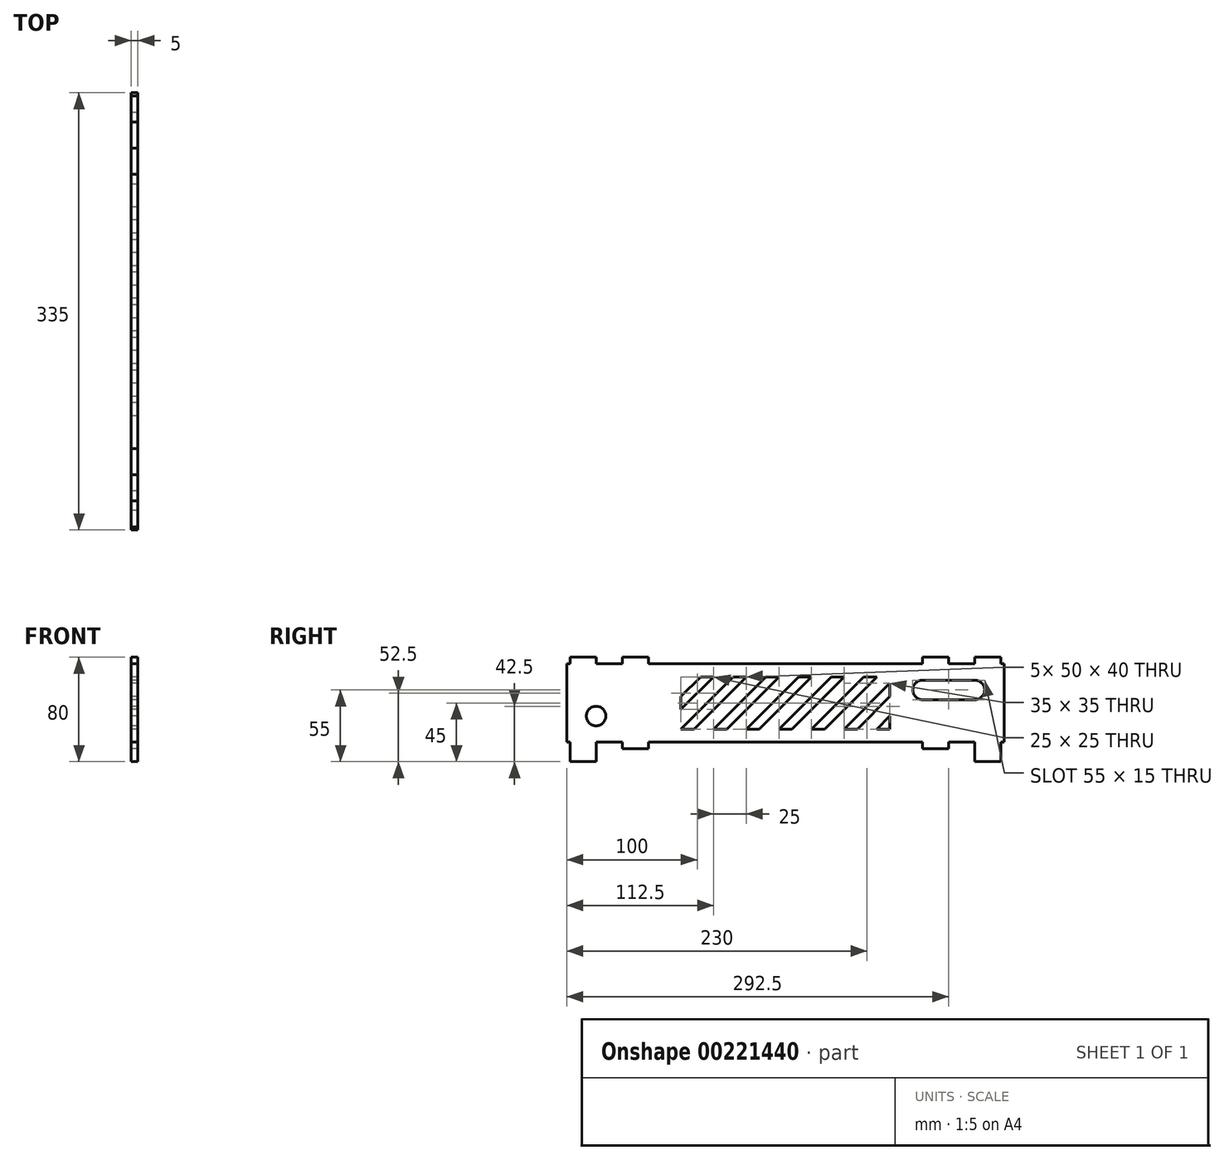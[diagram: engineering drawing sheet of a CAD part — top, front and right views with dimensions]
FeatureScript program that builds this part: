
annotation { "Feature Type Name" : "Feature", "Feature Type Description" : "" }
export const myFeature = defineFeature(function(context is Context, id is Id, definition is map)
    precondition{}
    {
        {
            assignVariable(context, id + "F0", {"name" : "thickness", "anyValue" : 5 * mm});
        }
        {
            var Q0;
            Q0=qCreatedBy(makeId("Right.planeOp"),FACE);
            var sketch = newSketch(context, id + "F1", { "sketchPlane" : qUnion([Q0])});
            skLineSegment(sketch, "E0.bottom", {"start": v(0, 0) * mm, "end": v(335, 0) * mm});
            skLineSegment(sketch, "E0.top", {"start": v(0, 60) * mm, "end": v(335, 60) * mm});
            skLineSegment(sketch, "E0.left", {"start": v(0, 0) * mm, "end": v(0, 60) * mm});
            skLineSegment(sketch, "E0.right", {"start": v(335, 0) * mm, "end": v(335, 60) * mm});
            skLineSegment(sketch, "E1", {"start": v(332.5, 0) * mm, "end": v(332.5, -15) * mm});
            skLineSegment(sketch, "E2", {"start": v(332.5, -15) * mm, "end": v(312.5, -15) * mm});
            skLineSegment(sketch, "E3", {"start": v(312.5, -15) * mm, "end": v(312.5, 0) * mm});
            skLineSegment(sketch, "E4", {"start": v(292.5, 0) * mm, "end": v(292.5, -5) * mm});
            skLineSegment(sketch, "E5", {"start": v(292.5, -5) * mm, "end": v(272.5, -5) * mm});
            skLineSegment(sketch, "E6", {"start": v(272.5, -5) * mm, "end": v(272.5, 0) * mm});
            skLineSegment(sketch, "E7", {"start": v(167.5, 60) * mm, "end": v(167.5, 0) * mm, "construction": true});
            skLineSegment(sketch, "E8", {"start": v(0, 30) * mm, "end": v(335, 30) * mm, "construction": true});
            skLineSegment(sketch, "E9.MirrorCS", {"start": v(62.5, -5) * mm, "end": v(62.5, 0) * mm});
            skLineSegment(sketch, "E10.MirrorCS", {"start": v(42.5, 0) * mm, "end": v(42.5, -5) * mm});
            skLineSegment(sketch, "E11.MirrorCS", {"start": v(42.5, -5) * mm, "end": v(62.5, -5) * mm});
            skLineSegment(sketch, "E12.MirrorCS", {"start": v(2.5, 0) * mm, "end": v(2.5, -15) * mm});
            skLineSegment(sketch, "E13.MirrorCS", {"start": v(2.5, -15) * mm, "end": v(22.5, -15) * mm});
            skLineSegment(sketch, "E14.MirrorCS", {"start": v(22.5, -15) * mm, "end": v(22.5, 0) * mm});
            skLineSegment(sketch, "E15.MirrorCS", {"start": v(62.5, 65) * mm, "end": v(62.5, 60) * mm});
            skLineSegment(sketch, "E16.MirrorCS", {"start": v(42.5, 60) * mm, "end": v(42.5, 65) * mm});
            skLineSegment(sketch, "E17.MirrorCS", {"start": v(42.5, 65) * mm, "end": v(62.5, 65) * mm});
            skLineSegment(sketch, "E18.MirrorCS", {"start": v(272.5, 65) * mm, "end": v(272.5, 60) * mm});
            skLineSegment(sketch, "E19.MirrorCS", {"start": v(292.5, 60) * mm, "end": v(292.5, 65) * mm});
            skLineSegment(sketch, "E20.MirrorCS", {"start": v(292.5, 65) * mm, "end": v(272.5, 65) * mm});
            skLineSegment(sketch, "E21", {"start": v(2.5, 60) * mm, "end": v(2.5, 65) * mm});
            skLineSegment(sketch, "E22", {"start": v(2.5, 65) * mm, "end": v(22.5, 65) * mm});
            skLineSegment(sketch, "E23", {"start": v(22.5, 65) * mm, "end": v(22.5, 60) * mm});
            skLineSegment(sketch, "E24.MirrorCS", {"start": v(332.5, 65) * mm, "end": v(312.5, 65) * mm});
            skLineSegment(sketch, "E25.MirrorCS", {"start": v(312.5, 65) * mm, "end": v(312.5, 60) * mm});
            skLineSegment(sketch, "E26.MirrorCS", {"start": v(332.5, 60) * mm, "end": v(332.5, 65) * mm});
            skLineSegment(sketch, "E27", {"start": v(272.5, 40) * mm, "end": v(312.5, 40) * mm, "construction": true});
            skArc(sketch, "E28.0.startCap", {"start": v(272.5, 32.5) * mm, "mid": v(265, 40) * mm, "end": v(272.5, 47.5) * mm});
            skArc(sketch, "E28.0.endCap", {"start": v(312.5, 47.5) * mm, "mid": v(320, 40) * mm, "end": v(312.5, 32.5) * mm});
            skLineSegment(sketch, "E28.0.left", {"start": v(272.5, 47.5) * mm, "end": v(312.5, 47.5) * mm});
            skLineSegment(sketch, "E28.0.right", {"start": v(272.5, 32.5) * mm, "end": v(312.5, 32.5) * mm});
            skCircle(sketch, "E29", {"center": v(22.5, 20) * mm, "radius": 7.5 * mm});
            skLineSegment(sketch, "E30.bottom", {"start": v(87.5, 50) * mm, "end": v(247.5, 50) * mm, "construction": true});
            skLineSegment(sketch, "E30.top", {"start": v(87.5, 10) * mm, "end": v(247.5, 10) * mm, "construction": true});
            skLineSegment(sketch, "E30.left", {"start": v(87.5, 50) * mm, "end": v(87.5, 10) * mm, "construction": true});
            skLineSegment(sketch, "E30.right", {"start": v(247.5, 50) * mm, "end": v(247.5, 10) * mm, "construction": true});
            skPoint(sketch, "E31", {"position": v(167.5, 50) * mm});
            skPoint(sketch, "E32", {"position": v(87.5, 30) * mm});
            skLineSegment(sketch, "E33", {"start": v(87.5, 10) * mm, "end": v(127.5, 50) * mm});
            skLineSegment(sketch, "E34", {"start": v(127.5, 50) * mm, "end": v(137.5, 50) * mm});
            skLineSegment(sketch, "E35", {"start": v(137.5, 50) * mm, "end": v(97.5, 10) * mm});
            skLineSegment(sketch, "E36", {"start": v(97.5, 10) * mm, "end": v(87.5, 10) * mm});
            skLineSegment(sketch, "E37.1.0.0", {"start": v(112.5, 10) * mm, "end": v(152.5, 50) * mm});
            skLineSegment(sketch, "E37.1.0.1", {"start": v(162.5, 50) * mm, "end": v(122.5, 10) * mm});
            skLineSegment(sketch, "E37.1.0.2", {"start": v(152.5, 50) * mm, "end": v(162.5, 50) * mm});
            skLineSegment(sketch, "E37.1.0.3", {"start": v(122.5, 10) * mm, "end": v(112.5, 10) * mm});
            skLineSegment(sketch, "E37.2.0.0", {"start": v(137.5, 10) * mm, "end": v(177.5, 50) * mm});
            skLineSegment(sketch, "E37.2.0.1", {"start": v(187.5, 50) * mm, "end": v(147.5, 10) * mm});
            skLineSegment(sketch, "E37.2.0.2", {"start": v(177.5, 50) * mm, "end": v(187.5, 50) * mm});
            skLineSegment(sketch, "E37.2.0.3", {"start": v(147.5, 10) * mm, "end": v(137.5, 10) * mm});
            skLineSegment(sketch, "E37.3.0.0", {"start": v(162.5, 10) * mm, "end": v(202.5, 50) * mm});
            skLineSegment(sketch, "E37.3.0.1", {"start": v(212.5, 50) * mm, "end": v(172.5, 10) * mm});
            skLineSegment(sketch, "E37.3.0.2", {"start": v(202.5, 50) * mm, "end": v(212.5, 50) * mm});
            skLineSegment(sketch, "E37.3.0.3", {"start": v(172.5, 10) * mm, "end": v(162.5, 10) * mm});
            skLineSegment(sketch, "E37.4.0.0", {"start": v(187.5, 10) * mm, "end": v(227.5, 50) * mm});
            skLineSegment(sketch, "E37.4.0.1", {"start": v(237.5, 50) * mm, "end": v(197.5, 10) * mm});
            skLineSegment(sketch, "E37.4.0.2", {"start": v(227.5, 50) * mm, "end": v(237.5, 50) * mm});
            skLineSegment(sketch, "E37.4.0.3", {"start": v(197.5, 10) * mm, "end": v(187.5, 10) * mm});
            skLineSegment(sketch, "E37.5.0.0", {"start": v(212.5, 10) * mm, "end": v(247.5, 45) * mm});
            skLineSegment(sketch, "E37.5.0.1", {"start": v(247.5, 35) * mm, "end": v(222.5, 10) * mm});
            skLineSegment(sketch, "E37.5.0.3", {"start": v(222.5, 10) * mm, "end": v(212.5, 10) * mm});
            skLineSegment(sketch, "E37.6.0.0", {"start": v(237.5, 10) * mm, "end": v(247.5, 20) * mm});
            skLineSegment(sketch, "E37.6.0.3", {"start": v(247.5, 10) * mm, "end": v(237.5, 10) * mm});
            skLineSegment(sketch, "E37.direction1", {"start": v(87.5, 10) * mm, "end": v(112.5, 10) * mm, "construction": true});
            skLineSegment(sketch, "E38.1.0.1", {"start": v(112.5, 50) * mm, "end": v(87.5, 25) * mm});
            skLineSegment(sketch, "E38.1.0.2", {"start": v(102.5, 50) * mm, "end": v(112.5, 50) * mm});
            skLineSegment(sketch, "E38.direction1", {"start": v(87.5, 10) * mm, "end": v(62.5, 10) * mm, "construction": true});
            skLineSegment(sketch, "E39.trimOffspring", {"start": v(87.5, 35) * mm, "end": v(102.5, 50) * mm});
            skLineSegment(sketch, "E40", {"start": v(87.5, 35) * mm, "end": v(87.5, 25) * mm});
            skLineSegment(sketch, "E41", {"start": v(247.5, 45) * mm, "end": v(247.5, 35) * mm});
            skLineSegment(sketch, "E42", {"start": v(247.5, 20) * mm, "end": v(247.5, 10) * mm});
            skSolve(sketch);
        }
        {
            var Q0;
            Q0 = qSketchRegion(id + "F1", true);
            extrude(context, id + "F2", {"entities" : qUnion([Q0]), "depth" : getVariable(context, 'thickness')});
        }
    });
